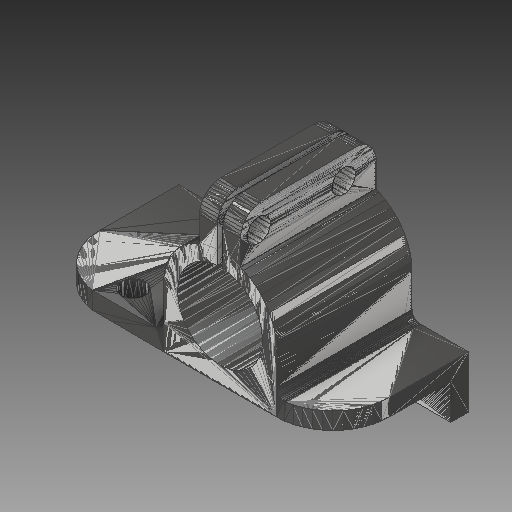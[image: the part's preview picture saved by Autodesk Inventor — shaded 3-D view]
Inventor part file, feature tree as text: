
AUTODESK INVENTOR PART (.ipt)
format: ipt  version: 2018 (Build 220112000, 112)  size: 662,016 bytes
history: native  units: mm
features: other x3, sketch x3, projected_geometry x2, extrude x1, hole x1
ambient origin geometry x8: Origin, YZ Plane, XZ Plane, XY Plane, X Axis, Y Axis, Z Axis, Center Point
bodies: Solid1 (feature_tree)
feature tree (10):
  other  "Z Endstop Holder"
  other  "MeshFeature1:1"
  sketch  "Sketch1"  dims[d0=12.0mm d1=10.0mm d2=0.0mm]
  extrude  "Extrusion1"  Depth=10.0mm TaperAngle=0.0deg
  hole  "Hole1"  [1 undecoded]
  sketch  "Sketch2"  dims[d3=3.3mm d4=6.0mm d5=4.0mm d6=2.0mm d7=90.0deg d8=8.0mm d9=20.594885mm]
  projected_geometry  "Projected Loop1"
  sketch  "Sketch3"
  projected_geometry  "Projected Loop2"
  other  "MeshFeature1"
note: 1 required parameter value undecoded (feature->parameter linkage not recoverable at this tier; creation-order binding heuristic only, values carry confidence <= 0.55)
